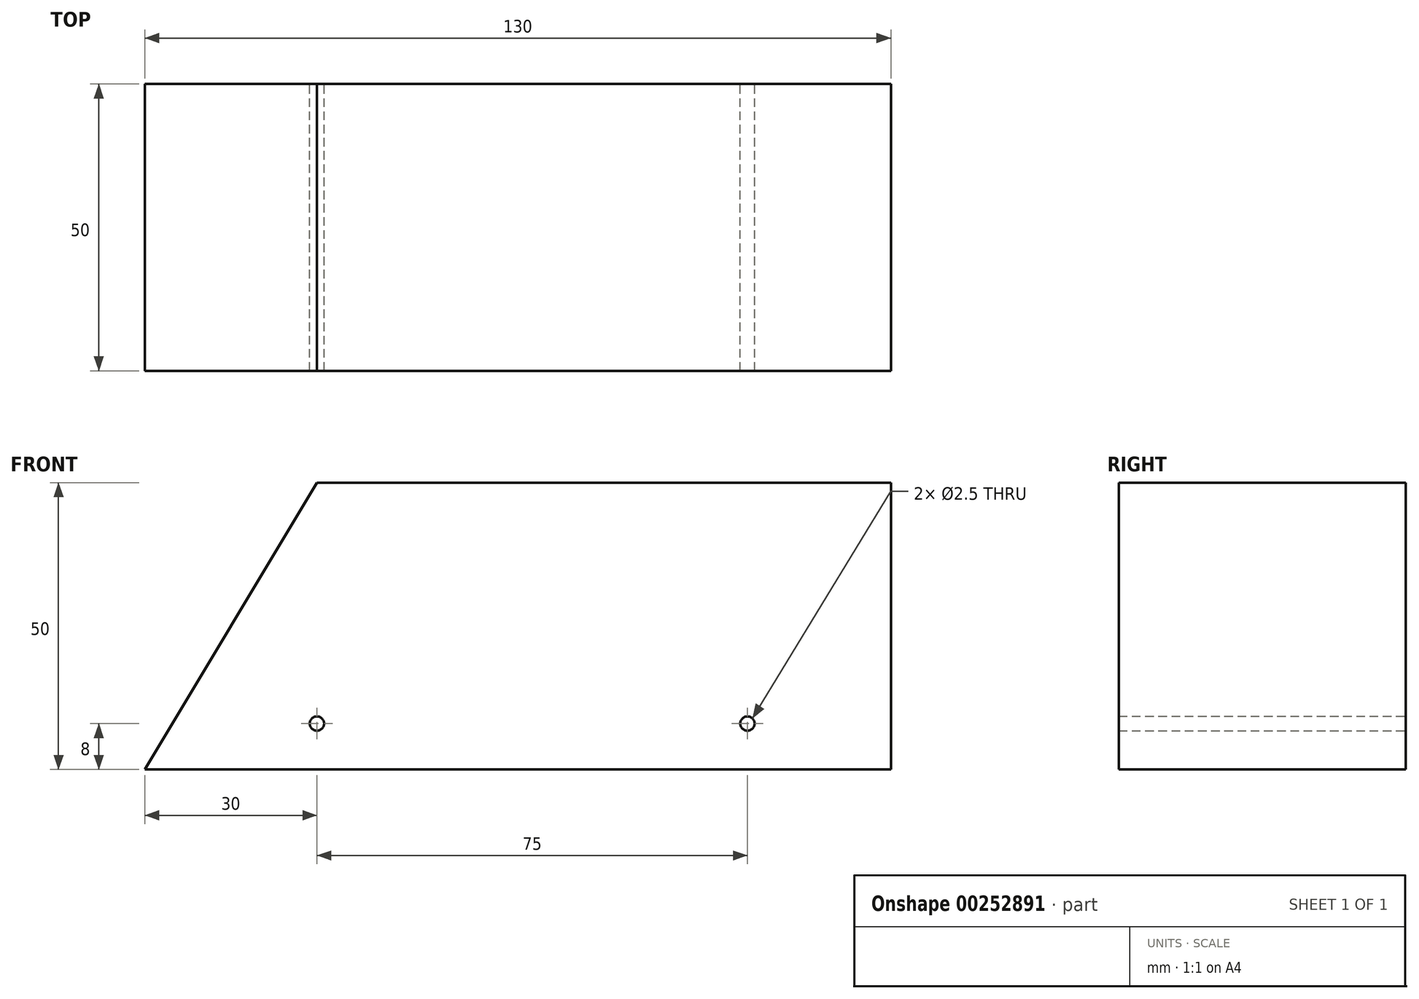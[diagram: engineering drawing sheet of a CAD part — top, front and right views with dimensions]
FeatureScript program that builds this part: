
annotation { "Feature Type Name" : "Feature", "Feature Type Description" : "" }
export const myFeature = defineFeature(function(context is Context, id is Id, definition is map)
    precondition{}
    {
        {
            var Q0;
            Q0=qCreatedBy(makeId("Front.planeOp"),FACE);
            var sketch = newSketch(context, id + "F0", { "sketchPlane" : qUnion([Q0])});
            skLineSegment(sketch, "E0.bottom", {"start": v(50, -25) * mm, "end": v(-50, -25) * mm});
            skLineSegment(sketch, "E0.top", {"start": v(50, 25) * mm, "end": v(-50, 25) * mm});
            skLineSegment(sketch, "E0.left", {"start": v(50, -25) * mm, "end": v(50, 25) * mm});
            skPoint(sketch, "E0.middle", {"position": v(0, 0) * mm});
            skLineSegment(sketch, "E1", {"start": v(-50, -25) * mm, "end": v(-80, -25) * mm});
            skLineSegment(sketch, "E2", {"start": v(-80, -25) * mm, "end": v(-50, 25) * mm});
            skLineSegment(sketch, "E3", {"start": v(50, -25) * mm, "end": v(25, -25) * mm});
            skLineSegment(sketch, "E4", {"start": v(25, -18.25) * mm, "end": v(25, -17) * mm});
            skLineSegment(sketch, "E5", {"start": v(-50, -18.25) * mm, "end": v(-50, -17) * mm});
            skLineSegment(sketch, "E6", {"start": v(-50, -17) * mm, "end": v(-42, -17) * mm});
            skCircle(sketch, "E7", {"center": v(-50, -17) * mm, "radius": 1.25 * mm});
            skCircle(sketch, "E8", {"center": v(25, -17) * mm, "radius": 1.25 * mm});
            skSolve(sketch);
        }
        {
            var Q0;
            Q0=makeQuery(id+"F0.imprint","IMPRINT",FACE,{"disambiguationData":[TD([[makeQuery(id+"F0.imprint","IMPRINT",EDGE,{"derivedFrom":sQuery(id+"F0.wireOp",EDGE,"E0.bottom")}),-1.0]])]});
            extrude(context, id + "F1", {"entities" : qUnion([Q0]), "depth" : 50 * mm});
        }
    });
